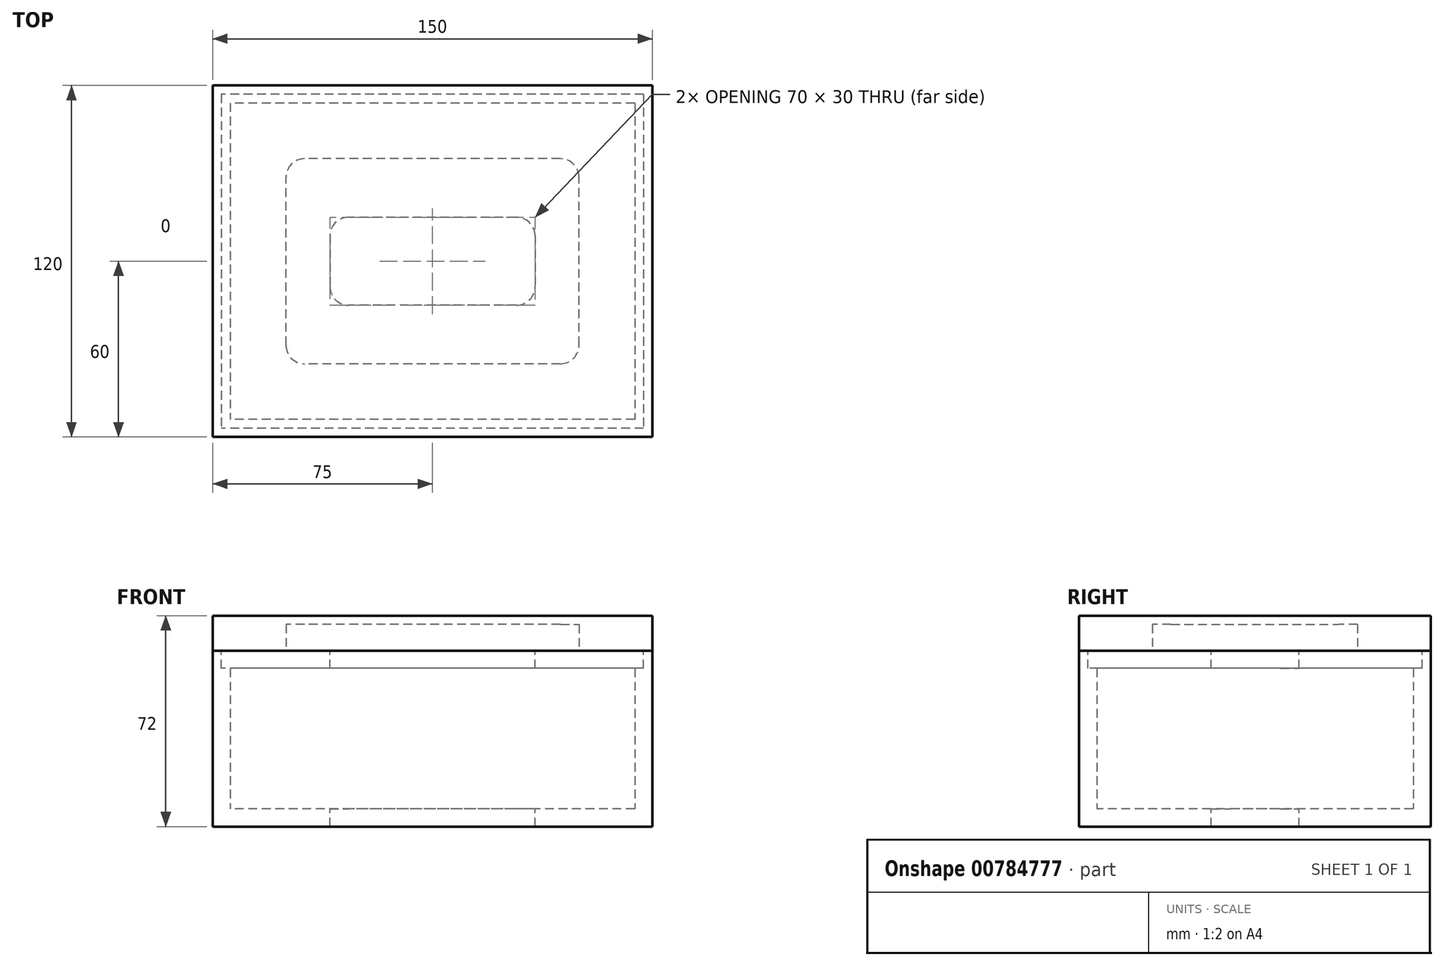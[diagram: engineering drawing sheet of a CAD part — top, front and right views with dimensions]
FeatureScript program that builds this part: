
annotation { "Feature Type Name" : "Feature", "Feature Type Description" : "" }
export const myFeature = defineFeature(function(context is Context, id is Id, definition is map)
    precondition{}
    {
        {
            var Q0;
            Q0=qCreatedBy(makeId("Top.planeOp"),FACE);
            var sketch = newSketch(context, id + "F0", { "sketchPlane" : qUnion([Q0])});
            skLineSegment(sketch, "E0.bottom", {"start": v(75, 60) * mm, "end": v(-75, 60) * mm});
            skLineSegment(sketch, "E0.top", {"start": v(75, -60) * mm, "end": v(-75, -60) * mm});
            skLineSegment(sketch, "E0.left", {"start": v(75, 60) * mm, "end": v(75, -60) * mm});
            skLineSegment(sketch, "E0.right", {"start": v(-75, 60) * mm, "end": v(-75, -60) * mm});
            skPoint(sketch, "E0.middle", {"position": v(0, 0) * mm});
            skSolve(sketch);
        }
        {
            var Q0;
            Q0 = qSketchRegion(id + "F0", true);
            extrude(context, id + "F1", {"entities" : qUnion([Q0]), "depth" : 60 * mm, "offsetDistance" : 25 * mm});
        }
        {
            var Q0;
            Q0=makeQuery(id+"F1.opExtrude","CAP_FACE",FACE,{"disambiguationData":[OSD([sQuery(id+"F0.wireOp",EDGE,"E0.bottom"),sQuery(id+"F0.wireOp",EDGE,"E0.top"),sQuery(id+"F0.wireOp",EDGE,"E0.left"),sQuery(id+"F0.wireOp",EDGE,"E0.right")])],"isStart":false});
            shell(context, id + "F2", {"entities" : qUnion([Q0]), "thickness" : 6 * mm});
        }
        {
            var Q0;
            Q0=makeQuery(id+"F1.opExtrude","CAP_FACE",FACE,{"disambiguationData":[OSD([sQuery(id+"F0.wireOp",EDGE,"E0.bottom"),sQuery(id+"F0.wireOp",EDGE,"E0.top"),sQuery(id+"F0.wireOp",EDGE,"E0.left"),sQuery(id+"F0.wireOp",EDGE,"E0.right")])],"isStart":false});
            var sketch = newSketch(context, id + "F3", { "sketchPlane" : qUnion([Q0])});
            skLineSegment(sketch, "E1.0", {"start": v(-72, 57) * mm, "end": v(-72, -57) * mm});
            skLineSegment(sketch, "E1.1", {"start": v(72, 57) * mm, "end": v(-72, 57) * mm});
            skLineSegment(sketch, "E1.2", {"start": v(72, 57) * mm, "end": v(72, -57) * mm});
            skLineSegment(sketch, "E1.3", {"start": v(72, -57) * mm, "end": v(-72, -57) * mm});
            skSolve(sketch);
        }
        {
            var Q0;
            Q0 = qSketchRegion(id + "F3", true);
            extrude(context, id + "F4", {"entities" : qUnion([Q0]), "operationType" : NewBodyOperationType.REMOVE, "oppositeDirection" : true, "depth" : 6 * mm, "offsetDistance" : 25 * mm});
        }
        {
            var Q0;
            Q0=makeQuery(id+"F4.boolean.opBoolean","COPY",FACE,{"derivedFrom":makeQuery(id+"F4.opExtrude","CAP_FACE",FACE,{"disambiguationData":[OSD([sQuery(id+"F3.wireOp",EDGE,"E1.0"),sQuery(id+"F3.wireOp",EDGE,"E1.1"),sQuery(id+"F3.wireOp",EDGE,"E1.2"),sQuery(id+"F3.wireOp",EDGE,"E1.3")])],"isStart":false})});
            var sketch = newSketch(context, id + "F5", { "sketchPlane" : qUnion([Q0])});
            skLineSegment(sketch, "E2.bottom", {"start": v(-72, 57) * mm, "end": v(72, 57) * mm});
            skLineSegment(sketch, "E2.top", {"start": v(-72, -57) * mm, "end": v(72, -57) * mm});
            skLineSegment(sketch, "E2.left", {"start": v(-72, 57) * mm, "end": v(-72, -57) * mm});
            skLineSegment(sketch, "E2.right", {"start": v(72, 57) * mm, "end": v(72, -57) * mm});
            skSolve(sketch);
        }
        {
            var Q0;
            Q0 = qSketchRegion(id + "F5", true);
            extrude(context, id + "F6", {"entities" : qUnion([Q0]), "depth" : 6 * mm, "offsetDistance" : 25 * mm});
        }
        {
            var Q0;
            Q0=makeQuery(id+"F6.opExtrude","CAP_FACE",FACE,{"disambiguationData":[OSD([sQuery(id+"F5.wireOp",EDGE,"E2.bottom"),sQuery(id+"F5.wireOp",EDGE,"E2.top"),sQuery(id+"F5.wireOp",EDGE,"E2.left"),sQuery(id+"F5.wireOp",EDGE,"E2.right")])],"isStart":false});
            var sketch = newSketch(context, id + "F7", { "sketchPlane" : qUnion([Q0])});
            skLineSegment(sketch, "E3.bottom", {"start": v(35, 15) * mm, "end": v(-35, 15) * mm});
            skLineSegment(sketch, "E3.top", {"start": v(35, -15) * mm, "end": v(-35, -15) * mm});
            skLineSegment(sketch, "E3.left", {"start": v(35, 15) * mm, "end": v(35, -15) * mm});
            skLineSegment(sketch, "E3.right", {"start": v(-35, 15) * mm, "end": v(-35, -15) * mm});
            skPoint(sketch, "E3.middle", {"position": v(0, 0) * mm});
            skSolve(sketch);
        }
        {
            var Q0;
            Q0 = qSketchRegion(id + "F7", true);
            extrude(context, id + "F8", {"entities" : qUnion([Q0]), "operationType" : NewBodyOperationType.REMOVE, "endBound" : BoundingType.THROUGH_ALL, "oppositeDirection" : true, "depth" : 25 * mm, "offsetDistance" : 25 * mm});
        }
        {
            var Q0;
            Q0=makeQuery(id+"F8.boolean.opBoolean","COPY",EDGE,{"derivedFrom":makeQuery(id+"F8.opExtrude","SWEPT_EDGE",EDGE,{"disambiguationData":[OSD([sQuery(id+"F7.wireOp",EDGE,"E3.bottom"),sQuery(id+"F7.wireOp",EDGE,"E3.right")])]})});
            var Q1;
            Q1=makeQuery(id+"F8.boolean.opBoolean","COPY",EDGE,{"derivedFrom":makeQuery(id+"F8.opExtrude","SWEPT_EDGE",EDGE,{"disambiguationData":[OSD([sQuery(id+"F7.wireOp",EDGE,"E3.bottom"),sQuery(id+"F7.wireOp",EDGE,"E3.left")])]})});
            var Q2;
            Q2=makeQuery(id+"F8.boolean.opBoolean","COPY",EDGE,{"derivedFrom":makeQuery(id+"F8.opExtrude","SWEPT_EDGE",EDGE,{"disambiguationData":[OSD([sQuery(id+"F7.wireOp",EDGE,"E3.top"),sQuery(id+"F7.wireOp",EDGE,"E3.right")])]})});
            var Q3;
            Q3=makeQuery(id+"F8.boolean.opBoolean","COPY",EDGE,{"derivedFrom":makeQuery(id+"F8.opExtrude","SWEPT_EDGE",EDGE,{"disambiguationData":[OSD([sQuery(id+"F7.wireOp",EDGE,"E3.top"),sQuery(id+"F7.wireOp",EDGE,"E3.left")])]})});
            fillet(context, id + "F9", {"entities" : qUnion([Q0, Q1, Q2, Q3]), "radius" : 6.35 * mm, "tangentPropagation" : true, "allowEdgeOverflow" : false});
        }
        {
            var Q0;
            Q0=makeQuery(id+"F1.opExtrude","CAP_FACE",FACE,{"disambiguationData":[OSD([sQuery(id+"F0.wireOp",EDGE,"E0.bottom"),sQuery(id+"F0.wireOp",EDGE,"E0.top"),sQuery(id+"F0.wireOp",EDGE,"E0.left"),sQuery(id+"F0.wireOp",EDGE,"E0.right")])],"isStart":false});
            var sketch = newSketch(context, id + "F10", { "sketchPlane" : qUnion([Q0])});
            skLineSegment(sketch, "E4.bottom", {"start": v(-75, 60) * mm, "end": v(75, 60) * mm});
            skLineSegment(sketch, "E4.top", {"start": v(-75, -60) * mm, "end": v(75, -60) * mm});
            skLineSegment(sketch, "E4.left", {"start": v(-75, 60) * mm, "end": v(-75, -60) * mm});
            skLineSegment(sketch, "E4.right", {"start": v(75, 60) * mm, "end": v(75, -60) * mm});
            skSolve(sketch);
        }
        {
            var Q0;
            Q0 = qSketchRegion(id + "F10", true);
            extrude(context, id + "F11", {"entities" : qUnion([Q0]), "depth" : 12 * mm, "offsetDistance" : 25 * mm});
        }
        {
            var Q0;
            Q0=makeQuery(id+"F11.opExtrude","CAP_FACE",FACE,{"disambiguationData":[OSD([sQuery(id+"F10.wireOp",EDGE,"E4.bottom"),sQuery(id+"F10.wireOp",EDGE,"E4.top"),sQuery(id+"F10.wireOp",EDGE,"E4.left"),sQuery(id+"F10.wireOp",EDGE,"E4.right")])],"isStart":true});
            var sketch = newSketch(context, id + "F12", { "sketchPlane" : qUnion([Q0])});
            skLineSegment(sketch, "E5.bottom", {"start": v(50, 35) * mm, "end": v(-50, 35) * mm});
            skLineSegment(sketch, "E5.top", {"start": v(50, -35) * mm, "end": v(-50, -35) * mm});
            skLineSegment(sketch, "E5.left", {"start": v(50, 35) * mm, "end": v(50, -35) * mm});
            skLineSegment(sketch, "E5.right", {"start": v(-50, 35) * mm, "end": v(-50, -35) * mm});
            skPoint(sketch, "E5.middle", {"position": v(0, 0) * mm});
            skSolve(sketch);
        }
        {
            var Q0;
            Q0 = qSketchRegion(id + "F12", true);
            extrude(context, id + "F13", {"entities" : qUnion([Q0]), "operationType" : NewBodyOperationType.REMOVE, "oppositeDirection" : true, "depth" : 9 * mm, "offsetDistance" : 25 * mm});
        }
        {
            var Q0;
            Q0=makeQuery(id+"F13.boolean.opBoolean","COPY",EDGE,{"derivedFrom":makeQuery(id+"F13.opExtrude","SWEPT_EDGE",EDGE,{"disambiguationData":[OSD([sQuery(id+"F12.wireOp",EDGE,"E5.top"),sQuery(id+"F12.wireOp",EDGE,"E5.right")])]})});
            var Q1;
            Q1=makeQuery(id+"F13.boolean.opBoolean","COPY",EDGE,{"derivedFrom":makeQuery(id+"F13.opExtrude","SWEPT_EDGE",EDGE,{"disambiguationData":[OSD([sQuery(id+"F12.wireOp",EDGE,"E5.bottom"),sQuery(id+"F12.wireOp",EDGE,"E5.right")])]})});
            var Q2;
            Q2=makeQuery(id+"F13.boolean.opBoolean","COPY",EDGE,{"derivedFrom":makeQuery(id+"F13.opExtrude","SWEPT_EDGE",EDGE,{"disambiguationData":[OSD([sQuery(id+"F12.wireOp",EDGE,"E5.bottom"),sQuery(id+"F12.wireOp",EDGE,"E5.left")])]})});
            var Q3;
            Q3=makeQuery(id+"F13.boolean.opBoolean","COPY",EDGE,{"derivedFrom":makeQuery(id+"F13.opExtrude","SWEPT_EDGE",EDGE,{"disambiguationData":[OSD([sQuery(id+"F12.wireOp",EDGE,"E5.top"),sQuery(id+"F12.wireOp",EDGE,"E5.left")])]})});
            fillet(context, id + "F14", {"entities" : qUnion([Q0, Q1, Q2, Q3]), "radius" : 6.35 * mm, "tangentPropagation" : true, "allowEdgeOverflow" : false});
        }
    });
